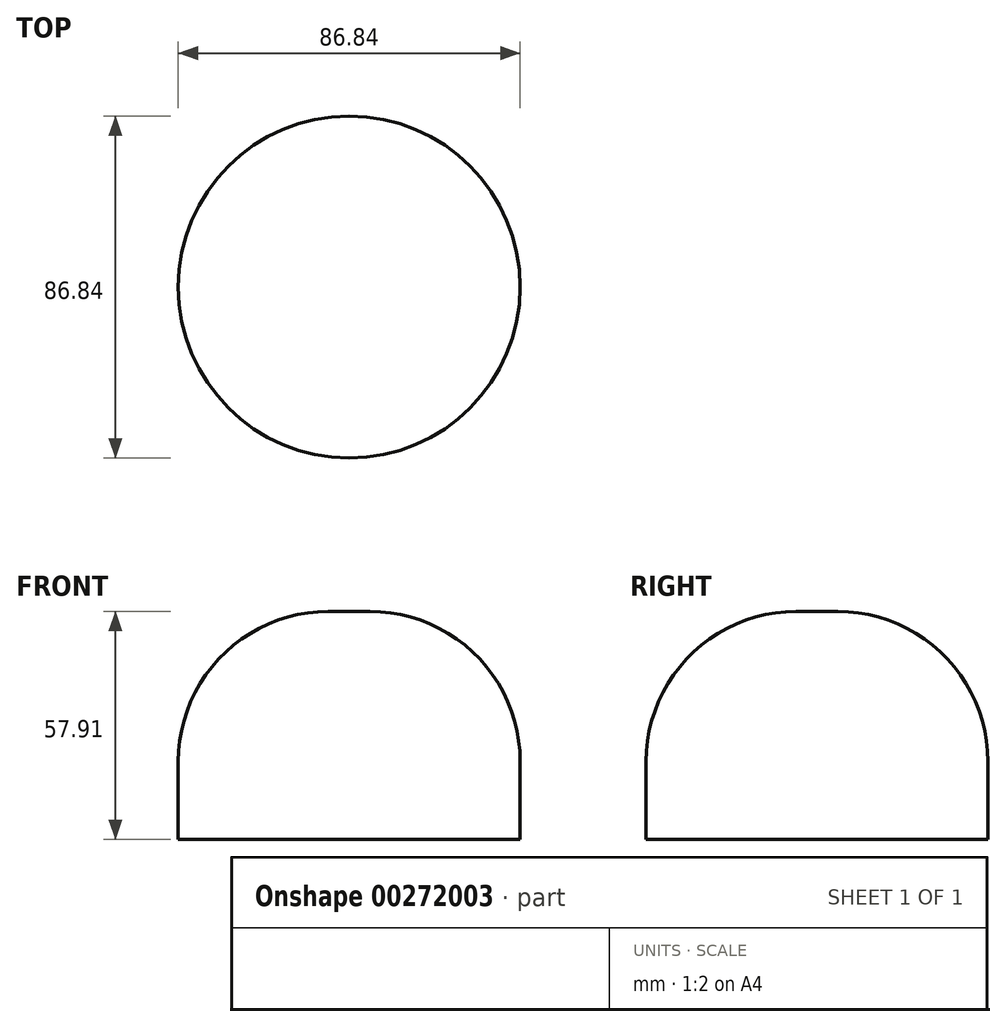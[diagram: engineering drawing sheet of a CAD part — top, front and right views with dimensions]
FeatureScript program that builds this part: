
annotation { "Feature Type Name" : "Feature", "Feature Type Description" : "" }
export const myFeature = defineFeature(function(context is Context, id is Id, definition is map)
    precondition{}
    {
        {
            var Q0;
            Q0=qCreatedBy(makeId("Top.planeOp"),FACE);
            var sketch = newSketch(context, id + "F0", { "sketchPlane" : qUnion([Q0])});
            skCircle(sketch, "E0", {"center": v(0, 0) * mm, "radius": 43.42 * mm});
            skSolve(sketch);
        }
        {
            var Q0;
            Q0 = qSketchRegion(id + "F0", true);
            extrude(context, id + "F1", {"entities" : qUnion([Q0]), "depth" : 25.4 * mm});
        }
        {
            var Q0;
            Q0=makeQuery(id+"F1.opExtrude","CAP_FACE",FACE,{"disambiguationData":[OSD([sQuery(id+"F0.wireOp",EDGE,"E0")])],"isStart":false});
            extrude(context, id + "F2", {"entities" : qUnion([Q0]), "operationType" : NewBodyOperationType.ADD, "depth" : 32.5 * mm});
        }
        {
            var Q0;
            Q0=makeQuery(id+"F2.opExtrude","CAP_EDGE",EDGE,{"disambiguationData":[OSD([sQuery(id+"F0.wireOp",EDGE,"E0")])],"isStart":false});
            fillet(context, id + "F3", {"entities" : qUnion([Q0]), "radius" : 38.1 * mm, "tangentPropagation" : true, "allowEdgeOverflow" : false});
        }
    });
